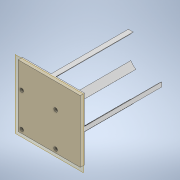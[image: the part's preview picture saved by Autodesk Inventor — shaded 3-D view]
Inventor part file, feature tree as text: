
AUTODESK INVENTOR PART (.ipt)
format: ipt  version: 2020 (Build 240168000, 168)  size: 137,728 bytes
history: native  units: mm
features: extrude x2, sketch x2
ambient origin geometry x8: Origin, YZ Plane, XZ Plane, XY Plane, X Axis, Y Axis, Z Axis, Center Point
bodies: Solid1 (feature_tree)
feature tree (4):
  extrude  "Extrusion1"  Depth=86.0mm
  extrude  "Extrusion2"  Depth=107.0mm
  sketch  "Sketch1"  dims[d0=86.0mm d1=86.0mm]
  sketch  "Sketch2"  dims[d2=5.0mm d3=5.0mm d4=5.0mm d5=113.0mm d6=0.0mm d7=107.0mm d8=0.0mm]
